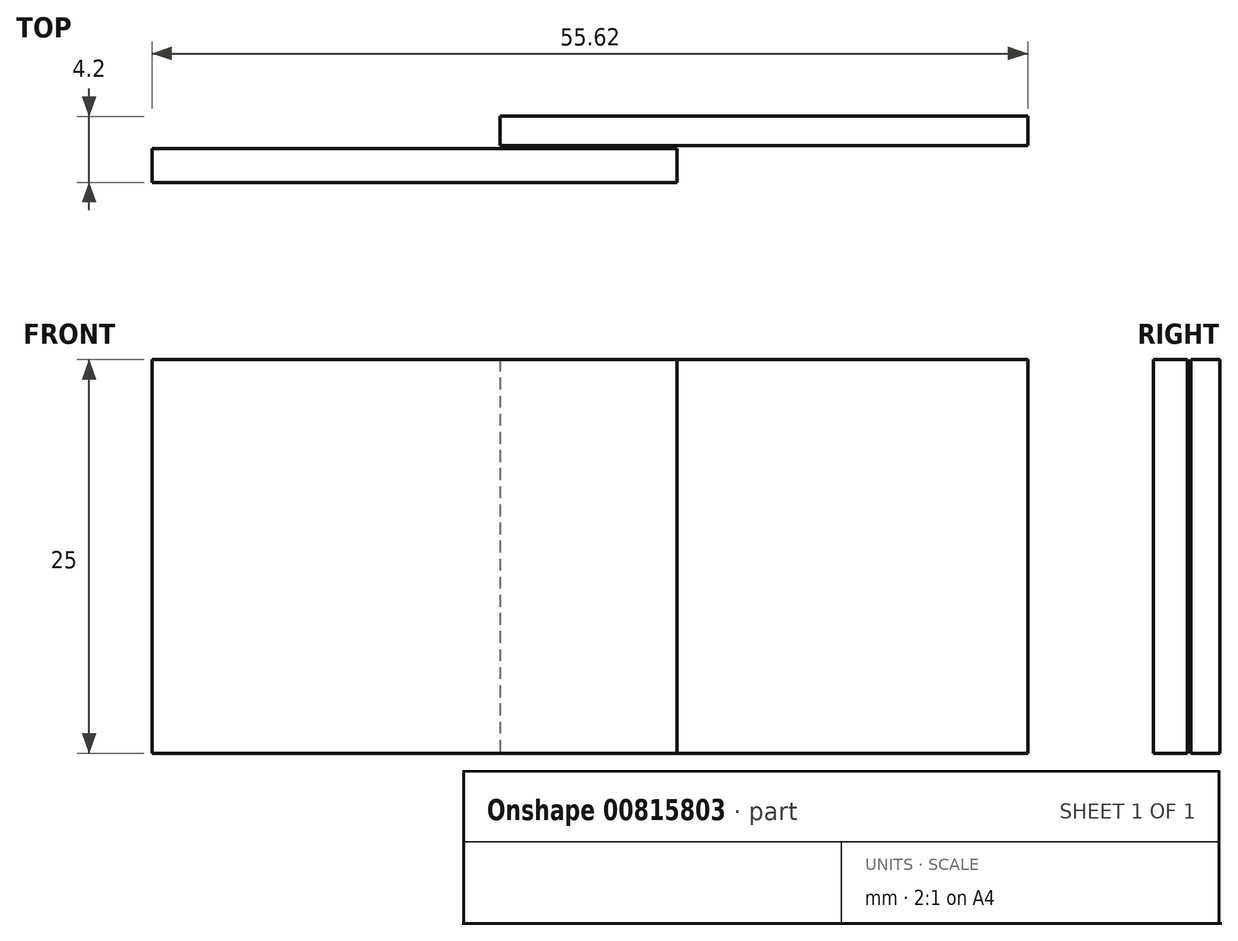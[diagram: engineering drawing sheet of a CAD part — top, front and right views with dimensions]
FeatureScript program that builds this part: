
annotation { "Feature Type Name" : "Feature", "Feature Type Description" : "" }
export const myFeature = defineFeature(function(context is Context, id is Id, definition is map)
    precondition{}
    {
        {
            var Q0;
            Q0=qCreatedBy(makeId("Top.planeOp"),FACE);
            var sketch = newSketch(context, id + "F0", { "sketchPlane" : qUnion([Q0])});
            skLineSegment(sketch, "E0.bottom", {"start": v(-33.35, 14.97) * mm, "end": v(0, 14.97) * mm});
            skLineSegment(sketch, "E0.top", {"start": v(-33.35, 17.12) * mm, "end": v(0, 17.12) * mm});
            skLineSegment(sketch, "E0.left", {"start": v(-33.35, 14.97) * mm, "end": v(-33.35, 17.12) * mm});
            skLineSegment(sketch, "E0.right", {"start": v(0, 14.97) * mm, "end": v(0, 17.12) * mm});
            skSolve(sketch);
        }
        {
            var Q0;
            Q0=qCreatedBy(makeId("Top.planeOp"),FACE);
            var sketch = newSketch(context, id + "F1", { "sketchPlane" : qUnion([Q0])});
            skLineSegment(sketch, "E1.bottom", {"start": v(-11.26, 17.33) * mm, "end": v(22.27, 17.33) * mm});
            skLineSegment(sketch, "E1.top", {"start": v(-11.26, 19.17) * mm, "end": v(22.27, 19.17) * mm});
            skLineSegment(sketch, "E1.left", {"start": v(-11.26, 17.33) * mm, "end": v(-11.26, 19.17) * mm});
            skLineSegment(sketch, "E1.right", {"start": v(22.27, 17.33) * mm, "end": v(22.27, 19.17) * mm});
            skSolve(sketch);
        }
        {
            var Q0;
            Q0=makeQuery(id+"F1.imprint","IMPRINT",FACE,{"disambiguationData":[TD([[makeQuery(id+"F1.imprint","IMPRINT",EDGE,{"derivedFrom":sQuery(id+"F1.wireOp",EDGE,"E1.bottom")}),1.0]])]});
            extrude(context, id + "F2", {"entities" : qUnion([Q0]), "depth" : 25 * mm, "offsetDistance" : 25 * mm});
        }
        {
            var Q0;
            Q0=makeQuery(id+"F0.imprint","IMPRINT",FACE,{"disambiguationData":[TD([[makeQuery(id+"F0.imprint","IMPRINT",EDGE,{"derivedFrom":sQuery(id+"F0.wireOp",EDGE,"E0.bottom")}),1.0]])]});
            extrude(context, id + "F3", {"entities" : qUnion([Q0]), "depth" : 25 * mm, "offsetDistance" : 25 * mm});
        }
    });
